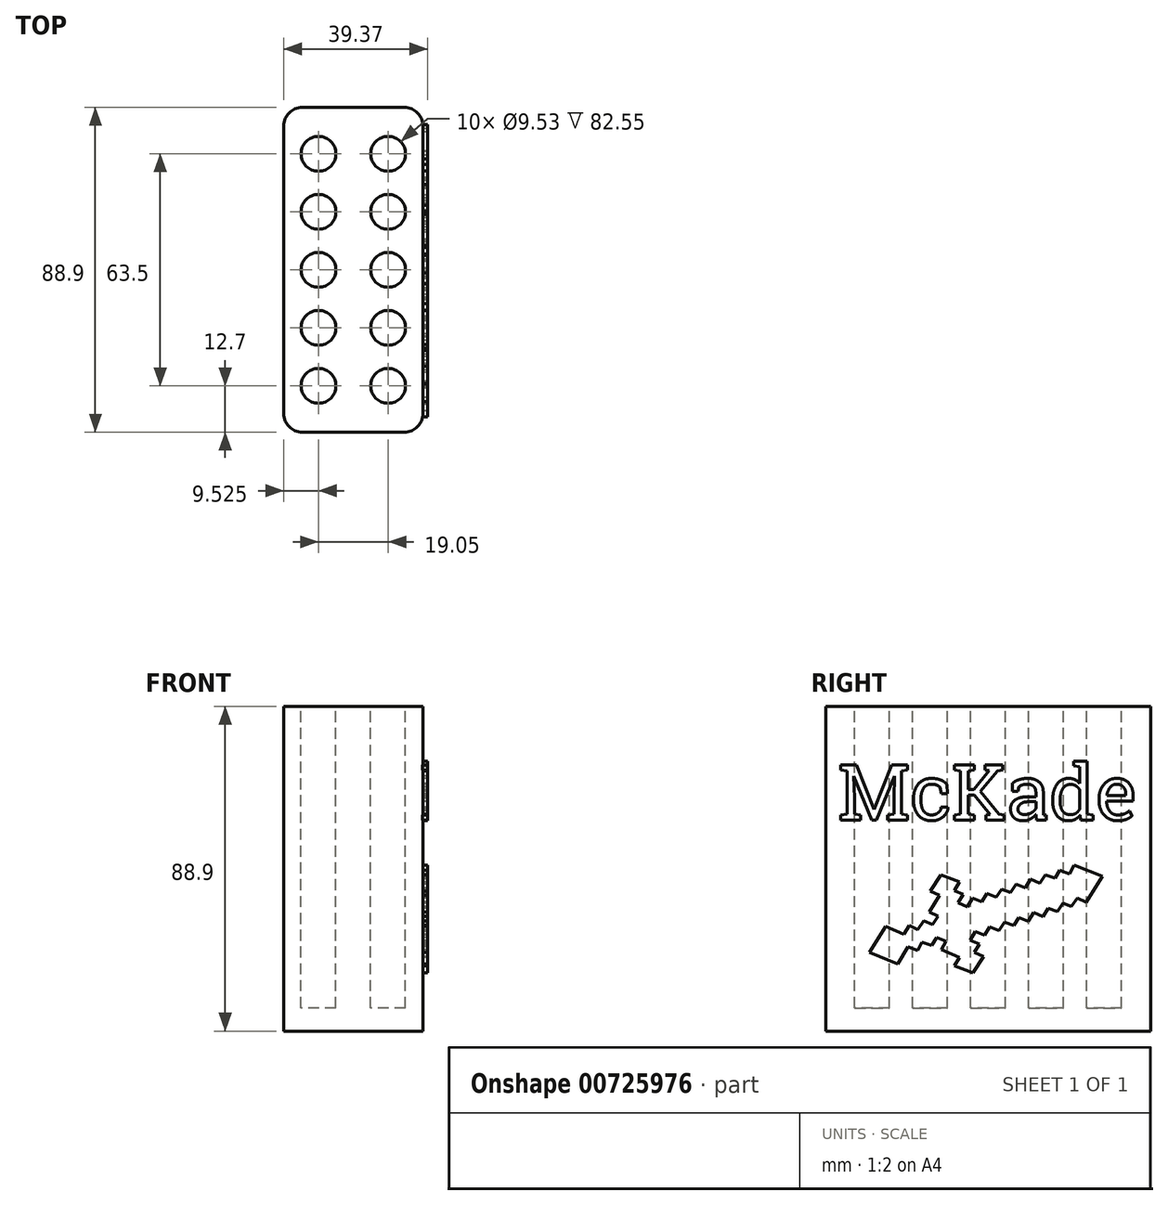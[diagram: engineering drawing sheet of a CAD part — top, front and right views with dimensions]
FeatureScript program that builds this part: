
annotation { "Feature Type Name" : "Feature", "Feature Type Description" : "" }
export const myFeature = defineFeature(function(context is Context, id is Id, definition is map)
    precondition{}
    {
        {
            var Q0;
            Q0=qCreatedBy(makeId("Right.planeOp"),FACE);
            var sketch = newSketch(context, id + "F0", { "sketchPlane" : qUnion([Q0])});
            skLineSegment(sketch, "E0.bottom", {"start": v(-44.45, 44.45) * mm, "end": v(44.45, 44.45) * mm});
            skLineSegment(sketch, "E0.top", {"start": v(-44.45, -44.45) * mm, "end": v(44.45, -44.45) * mm});
            skLineSegment(sketch, "E0.left", {"start": v(-44.45, 44.45) * mm, "end": v(-44.45, -44.45) * mm});
            skLineSegment(sketch, "E0.right", {"start": v(44.45, 44.45) * mm, "end": v(44.45, -44.45) * mm});
            skPoint(sketch, "E0.middle", {"position": v(0, 0) * mm});
            skSolve(sketch);
        }
        {
            var Q0;
            Q0=qSketchRegion(id+"F0",true);
            extrude(context, id + "F1", {"entities" : qUnion([Q0]), "endBound" : BoundingType.SYMMETRIC, "depth" : 38.1 * mm, "offsetDistance" : 25.4 * mm});
        }
        {
            var Q0;
            Q0=makeQuery(id+"F1.opExtrude","SWEPT_FACE",FACE,{"disambiguationData":[OSD([sQuery(id+"F0.wireOp",EDGE,"E0.bottom")])]});
            var sketch = newSketch(context, id + "F2", { "sketchPlane" : qUnion([Q0])});
            skCircle(sketch, "E1", {"center": v(-9.52, -31.75) * mm, "radius": 4.76 * mm});
            skCircle(sketch, "E2", {"center": v(-9.52, 0) * mm, "radius": 4.76 * mm});
            skCircle(sketch, "E3", {"center": v(-9.52, -15.88) * mm, "radius": 4.76 * mm});
            skCircle(sketch, "E4", {"center": v(-9.52, 15.88) * mm, "radius": 4.76 * mm});
            skCircle(sketch, "E5", {"center": v(-9.52, 31.75) * mm, "radius": 4.76 * mm});
            skCircle(sketch, "E6.MirrorC", {"center": v(9.52, 0) * mm, "radius": 4.76 * mm});
            skCircle(sketch, "E7.MirrorC", {"center": v(9.52, -31.75) * mm, "radius": 4.76 * mm});
            skCircle(sketch, "E8.MirrorC", {"center": v(9.52, -15.88) * mm, "radius": 4.76 * mm});
            skCircle(sketch, "E9.MirrorC", {"center": v(9.52, 15.88) * mm, "radius": 4.76 * mm});
            skCircle(sketch, "E10.MirrorC", {"center": v(9.52, 31.75) * mm, "radius": 4.76 * mm});
            skSolve(sketch);
        }
        {
            var Q0;
            Q0=qSketchRegion(id+"F2",true);
            extrude(context, id + "F3", {"entities" : qUnion([Q0]), "operationType" : NewBodyOperationType.REMOVE, "oppositeDirection" : true, "depth" : 82.55 * mm, "offsetDistance" : 25.4 * mm});
        }
        {
            var Q0;
            Q0=makeQuery(id+"F1.opExtrude","CAP_FACE",FACE,{"disambiguationData":[OSD([sQuery(id+"F0.wireOp",EDGE,"E0.bottom"),sQuery(id+"F0.wireOp",EDGE,"E0.top"),sQuery(id+"F0.wireOp",EDGE,"E0.left"),sQuery(id+"F0.wireOp",EDGE,"E0.right")])],"isStart":false});
            var sketch = newSketch(context, id + "F4", { "sketchPlane" : qUnion([Q0])});
            skText(sketch, "E11", { "text": "McKade", "fontName": "RobotoSlab-Regular.ttf"});
            const initialGuessF4  = {"E11": [-0.04104, 0.01333, 1, 0, 0.01524]};
            skSetInitialGuess(sketch, initialGuessF4);
            skSolve(sketch);
        }
        {
            var Q0;
            Q0=qSketchRegion(id+"F4",true);
            extrude(context, id + "F5", {"entities" : qUnion([Q0]), "operationType" : NewBodyOperationType.ADD, "depth" : 1.27 * mm, "offsetDistance" : 25.4 * mm});
        }
        {
            var Q0;
            Q0=makeQuery(id+"F1.opExtrude","CAP_EDGE",EDGE,{"disambiguationData":[OSD([sQuery(id+"F0.wireOp",EDGE,"E0.left")])],"isStart":false});
            var Q1;
            Q1=makeQuery(id+"F1.opExtrude","CAP_EDGE",EDGE,{"disambiguationData":[OSD([sQuery(id+"F0.wireOp",EDGE,"E0.right")])],"isStart":false});
            var Q2;
            Q2=makeQuery(id+"F1.opExtrude","CAP_EDGE",EDGE,{"disambiguationData":[OSD([sQuery(id+"F0.wireOp",EDGE,"E0.right")])],"isStart":true});
            var Q3;
            Q3=makeQuery(id+"F1.opExtrude","CAP_EDGE",EDGE,{"disambiguationData":[OSD([sQuery(id+"F0.wireOp",EDGE,"E0.left")])],"isStart":true});
            fillet(context, id + "F6", {"entities" : qUnion([Q0, Q1, Q2, Q3]), "radius" : 5.08 * mm, "tangentPropagation" : true, "allowEdgeOverflow" : false});
        }
        {
            var Q0;
            {var subQ0=sQuery(id+"F0.wireOp",EDGE,"E0.right");var subQ1=sQuery(id+"F0.wireOp",EDGE,"E0.left");var subQ2=sQuery(id+"F0.wireOp",EDGE,"E0.top");var subQ3=sQuery(id+"F0.wireOp",EDGE,"E0.bottom");Q0=makeQuery(id+"F5.boolean.opBoolean","SPLIT",FACE,{"disambiguationData":[TD([makeQuery(id+"F1.opExtrude","SWEPT_FACE",FACE,{"disambiguationData":[OSD([subQ3])]})])],"derivedFrom":makeQuery(id+"F1.opExtrude","CAP_FACE",FACE,{"disambiguationData":[OSD([subQ3,subQ2,subQ1,subQ0])],"isStart":false})});}
            var sketch = newSketch(context, id + "F7", { "sketchPlane" : qUnion([Q0])});
            skLineSegment(sketch, "E12", {"start": v(-32.42, -22.86) * mm, "end": v(-28.08, -15.8) * mm});
            skLineSegment(sketch, "E13", {"start": v(-28.08, -15.8) * mm, "end": v(-23.08, -17.92) * mm});
            skLineSegment(sketch, "E14", {"start": v(-23.08, -17.92) * mm, "end": v(-21.51, -15.52) * mm});
            skLineSegment(sketch, "E15", {"start": v(-21.51, -15.52) * mm, "end": v(-19.23, -16.64) * mm});
            skLineSegment(sketch, "E16", {"start": v(-19.23, -16.64) * mm, "end": v(-17.58, -14.33) * mm});
            skLineSegment(sketch, "E17", {"start": v(-17.58, -14.33) * mm, "end": v(-15.14, -15.3) * mm});
            skLineSegment(sketch, "E18", {"start": v(-15.14, -15.3) * mm, "end": v(-13.73, -12.96) * mm});
            skLineSegment(sketch, "E19", {"start": v(-13.73, -12.96) * mm, "end": v(-16.1, -11.86) * mm});
            skLineSegment(sketch, "E20", {"start": v(-16.1, -11.86) * mm, "end": v(-13.36, -7.3) * mm});
            skLineSegment(sketch, "E21", {"start": v(-13.36, -7.3) * mm, "end": v(-15.83, -6.2) * mm});
            skLineSegment(sketch, "E22", {"start": v(-15.83, -6.2) * mm, "end": v(-12.86, -1.67) * mm});
            skLineSegment(sketch, "E23", {"start": v(-12.86, -1.67) * mm, "end": v(-7.83, -3.58) * mm});
            skLineSegment(sketch, "E24", {"start": v(-7.83, -3.58) * mm, "end": v(-9.23, -5.95) * mm});
            skLineSegment(sketch, "E25", {"start": v(-9.23, -5.95) * mm, "end": v(-6.76, -7.02) * mm});
            skLineSegment(sketch, "E26", {"start": v(-6.76, -7.02) * mm, "end": v(-8.2, -9.36) * mm});
            skLineSegment(sketch, "E27", {"start": v(-8.2, -9.36) * mm, "end": v(-5.7, -10.49) * mm});
            skLineSegment(sketch, "E28", {"start": v(-5.7, -10.49) * mm, "end": v(-4.23, -8.11) * mm});
            skLineSegment(sketch, "E29", {"start": v(-4.23, -8.11) * mm, "end": v(-1.76, -9.11) * mm});
            skLineSegment(sketch, "E30", {"start": v(-1.76, -9.11) * mm, "end": v(-0.32, -6.8) * mm});
            skLineSegment(sketch, "E31", {"start": v(-0.32, -6.8) * mm, "end": v(2.24, -7.83) * mm});
            skLineSegment(sketch, "E32", {"start": v(2.24, -7.83) * mm, "end": v(3.77, -5.58) * mm});
            skLineSegment(sketch, "E33", {"start": v(3.77, -5.58) * mm, "end": v(6.14, -6.55) * mm});
            skLineSegment(sketch, "E34", {"start": v(6.14, -6.55) * mm, "end": v(7.61, -4.27) * mm});
            skLineSegment(sketch, "E35", {"start": v(7.61, -4.27) * mm, "end": v(10.24, -5.27) * mm});
            skLineSegment(sketch, "E36", {"start": v(10.24, -5.27) * mm, "end": v(11.64, -2.9) * mm});
            skLineSegment(sketch, "E37", {"start": v(11.64, -2.9) * mm, "end": v(14.18, -3.92) * mm});
            skLineSegment(sketch, "E38", {"start": v(14.18, -3.92) * mm, "end": v(15.65, -1.64) * mm});
            skLineSegment(sketch, "E39", {"start": v(15.65, -1.64) * mm, "end": v(18.3, -2.64) * mm});
            skLineSegment(sketch, "E40", {"start": v(18.3, -2.64) * mm, "end": v(19.58, -0.49) * mm});
            skLineSegment(sketch, "E41", {"start": v(19.58, -0.49) * mm, "end": v(22.24, -1.4) * mm});
            skLineSegment(sketch, "E42", {"start": v(22.24, -1.4) * mm, "end": v(23.55, 0.95) * mm});
            skLineSegment(sketch, "E43", {"start": v(23.55, 0.95) * mm, "end": v(31.33, -2.14) * mm});
            skLineSegment(sketch, "E44", {"start": v(-32.42, -22.86) * mm, "end": v(31.33, -2.14) * mm});
            skLineSegment(sketch, "E45.MirrorCS", {"start": v(26.86, -9.22) * mm, "end": v(31.33, -2.14) * mm});
            skLineSegment(sketch, "E46.MirrorCS", {"start": v(-4.9, -19.54) * mm, "end": v(-3.53, -17.16) * mm});
            skLineSegment(sketch, "E47.MirrorCS", {"start": v(8.37, -13.39) * mm, "end": v(10.9, -14.37) * mm});
            skLineSegment(sketch, "E48.MirrorCS", {"start": v(-3.72, -22.9) * mm, "end": v(-2.35, -20.6) * mm});
            skLineSegment(sketch, "E49.MirrorCS", {"start": v(18.94, -11.77) * mm, "end": v(20.5, -9.4) * mm});
            skLineSegment(sketch, "E50.MirrorCS", {"start": v(0.46, -15.96) * mm, "end": v(2.99, -16.99) * mm});
            skLineSegment(sketch, "E51.MirrorCS", {"start": v(-12.76, -22.17) * mm, "end": v(-7.85, -24.24) * mm});
            skLineSegment(sketch, "E52.MirrorCS", {"start": v(-11.48, -19.89) * mm, "end": v(-12.76, -22.17) * mm});
            skLineSegment(sketch, "E53.MirrorCS", {"start": v(-1.19, -24) * mm, "end": v(-3.72, -22.9) * mm});
            skLineSegment(sketch, "E54.MirrorCS", {"start": v(20.5, -9.4) * mm, "end": v(22.8, -10.4) * mm});
            skLineSegment(sketch, "E55.MirrorCS", {"start": v(-7.85, -24.24) * mm, "end": v(-9.2, -26.58) * mm});
            skLineSegment(sketch, "E56.MirrorCS", {"start": v(-14, -18.82) * mm, "end": v(-11.48, -19.89) * mm});
            skLineSegment(sketch, "E57.MirrorCS", {"start": v(2.99, -16.99) * mm, "end": v(4.45, -14.65) * mm});
            skLineSegment(sketch, "E58.MirrorCS", {"start": v(-15.4, -21.04) * mm, "end": v(-14, -18.82) * mm});
            skLineSegment(sketch, "E59.MirrorCS", {"start": v(-9.2, -26.58) * mm, "end": v(-4.14, -28.5) * mm});
            skLineSegment(sketch, "E60.MirrorCS", {"start": v(-18.1, -20.14) * mm, "end": v(-15.4, -21.04) * mm});
            skLineSegment(sketch, "E61.MirrorCS", {"start": v(-4.14, -28.5) * mm, "end": v(-1.19, -24) * mm});
            skLineSegment(sketch, "E62.MirrorCS", {"start": v(-19.28, -22.4) * mm, "end": v(-18.1, -20.14) * mm});
            skLineSegment(sketch, "E63.MirrorCS", {"start": v(-21.96, -21.36) * mm, "end": v(-19.28, -22.4) * mm});
            skLineSegment(sketch, "E64.MirrorCS", {"start": v(-24.76, -26.02) * mm, "end": v(-21.96, -21.36) * mm});
            skLineSegment(sketch, "E65.MirrorCS", {"start": v(-2.35, -20.6) * mm, "end": v(-4.9, -19.54) * mm});
            skLineSegment(sketch, "E66.MirrorCS", {"start": v(-3.53, -17.16) * mm, "end": v(-0.95, -18.22) * mm});
            skLineSegment(sketch, "E67.MirrorCS", {"start": v(10.9, -14.37) * mm, "end": v(12.43, -12.02) * mm});
            skLineSegment(sketch, "E68.MirrorCS", {"start": v(7.01, -15.57) * mm, "end": v(8.37, -13.39) * mm});
            skLineSegment(sketch, "E69.MirrorCS", {"start": v(12.43, -12.02) * mm, "end": v(14.97, -13.11) * mm});
            skLineSegment(sketch, "E70.MirrorCS", {"start": v(-0.95, -18.22) * mm, "end": v(0.46, -15.96) * mm});
            skLineSegment(sketch, "E71.MirrorCS", {"start": v(24.42, -8.1) * mm, "end": v(26.86, -9.22) * mm});
            skLineSegment(sketch, "E72.MirrorCS", {"start": v(4.45, -14.65) * mm, "end": v(7.01, -15.57) * mm});
            skLineSegment(sketch, "E73.MirrorCS", {"start": v(16.4, -10.79) * mm, "end": v(18.94, -11.77) * mm});
            skLineSegment(sketch, "E74.MirrorCS", {"start": v(14.97, -13.11) * mm, "end": v(16.4, -10.79) * mm});
            skLineSegment(sketch, "E75.MirrorCS", {"start": v(22.8, -10.4) * mm, "end": v(24.42, -8.1) * mm});
            skLineSegment(sketch, "E76.MirrorCS", {"start": v(-32.42, -22.86) * mm, "end": v(-24.76, -26.02) * mm});
            skSolve(sketch);
        }
        {
            var Q0;
            Q0=qSketchRegion(id+"F7",true);
            extrude(context, id + "F8", {"entities" : qUnion([Q0]), "operationType" : NewBodyOperationType.ADD, "depth" : 1.27 * mm, "offsetDistance" : 25.4 * mm});
        }
    });
